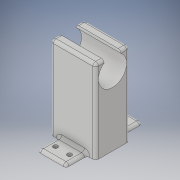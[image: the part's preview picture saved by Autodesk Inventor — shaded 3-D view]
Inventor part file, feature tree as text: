
AUTODESK INVENTOR PART (.ipt)
format: ipt  version: 2017 (Build 210142000, 142)  size: 405,504 bytes
history: native  units: in
note: dims shown in document units (in); Inventor stores cm internally (conversion verified against a paired STEP export)
features: fillet x14, extrude x4, sketch x4, projected_geometry x1
ambient origin geometry x8: Origin, YZ Plane, XZ Plane, XY Plane, X Axis, Y Axis, Z Axis, Center Point
bodies: Solid1 (feature_tree)
feature tree (23):
  extrude  "Extrusion1"  Depth=0.9449in
  extrude  "Extrusion2"  Depth=0.7874in
  extrude  "Extrusion3"  Depth=0.2953in
  extrude  "Extrusion4"  Depth=0.7874in
  fillet  "Fillet1"  Radius=0.0787in
  fillet  "Fillet2"  Radius=2.25in
  fillet  "Fillet3"  Radius=0.7874in
  fillet  "Fillet4"  Radius=0.3937in
  fillet  "Fillet5"  Radius=2.5in
  fillet  "Fillet6"  Radius=2.5in
  fillet  "Fillet7"  Radius=0.0787in
  fillet  "Fillet8"  Radius=0.0787in
  fillet  "Fillet9"  Radius=0.0787in
  fillet  "Fillet10"  Radius=0.0787in
  fillet  "Fillet11"  Radius=0.0787in
  fillet  "Fillet12"  Radius=0.0787in
  fillet  "Fillet13"  Radius=0.0787in
  fillet  "Fillet14"  Radius=0.0787in
  sketch  "Sketch1"  dims[d0=1.2598in d1=0.9449in]
  sketch  "Sketch2"  dims[d2=0.7874in d3=2.126in]
  sketch  "Sketch3"  dims[d4=0.125in d5=0.2953in]
  projected_geometry  "Projected Loop1"
  sketch  "Sketch4"  dims[d7=0.1969in d8=0.7874in d10=1.5354in d11=0.7874in d13=0.3937in d16=0.0787in d17=0.0in d18=2.25in d19=0.0in d20=0.7874in d21=0.3937in d22=2.5in d23=0.0in d24=2.5in d25=0.0in d26=0.0787in d27=0.0787in d28=0.0787in d29=0.0787in d30=0.0787in d31=0.0787in d32=0.0787in d33=0.0787in d34=0.0787in d35=0.0787in d36=0.0787in d37=0.0787in d38=0.0787in d39=0.0787in]
